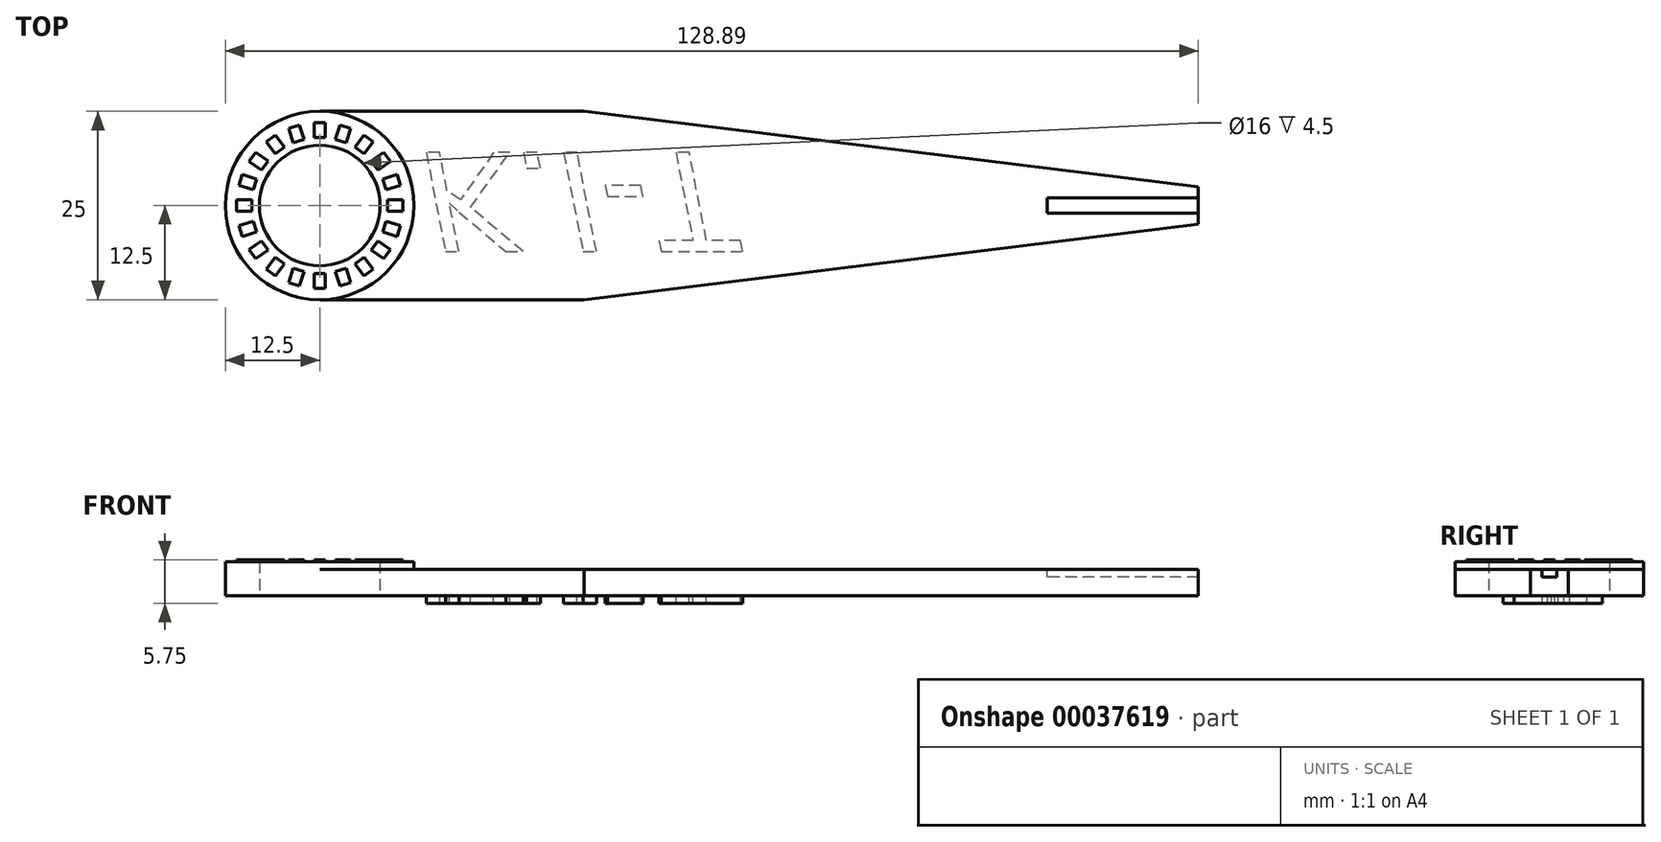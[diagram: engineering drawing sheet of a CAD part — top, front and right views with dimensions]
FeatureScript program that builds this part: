
annotation { "Feature Type Name" : "Feature", "Feature Type Description" : "" }
export const myFeature = defineFeature(function(context is Context, id is Id, definition is map)
    precondition{}
    {
        {
            var Q0;
            Q0=qCreatedBy(makeId("Top.planeOp"),FACE);
            var sketch = newSketch(context, id + "F0", { "sketchPlane" : qUnion([Q0])});
            skCircle(sketch, "E0", {"center": v(0, 0) * mm, "radius": 8 * mm});
            skCircle(sketch, "E1", {"center": v(0, 0) * mm, "radius": 12.5 * mm});
            skPoint(sketch, "E2", {"position": v(0, 12.5) * mm});
            skLineSegment(sketch, "E3", {"start": v(0, 12.5) * mm, "end": v(35, 12.5) * mm});
            skLineSegment(sketch, "E4", {"start": v(0, 0) * mm, "end": v(39.93, 0) * mm, "construction": true});
            skLineSegment(sketch, "E5.MirrorCS", {"start": v(0, -12.5) * mm, "end": v(35, -12.5) * mm});
            skLineSegment(sketch, "E6", {"start": v(35, 12.5) * mm, "end": v(89.7, 12.5) * mm, "construction": true});
            skLineSegment(sketch, "E7", {"start": v(35, 12.5) * mm, "end": v(116.39, 2.5) * mm});
            skLineSegment(sketch, "E8.MirrorCS", {"start": v(35, -12.5) * mm, "end": v(116.39, -2.5) * mm});
            skLineSegment(sketch, "E9", {"start": v(116.39, 2.5) * mm, "end": v(116.39, -2.5) * mm});
            skSolve(sketch);
        }
        {
            var Q0;
            Q0 = qSketchRegion(id + "F0", true);
            extrude(context, id + "F1", {"entities" : qUnion([Q0]), "depth" : 3.5 * mm});
        }
        {
            var Q0;
            Q0=makeQuery(id+"F1.opExtrude","CAP_FACE",FACE,{"disambiguationData":[OSD([sQuery(id+"F0.wireOp",EDGE,"E0"),sQuery(id+"F0.wireOp",EDGE,"E1"),sQuery(id+"F0.wireOp",EDGE,"E3"),sQuery(id+"F0.wireOp",EDGE,"E5.MirrorCS"),sQuery(id+"F0.wireOp",EDGE,"E7"),sQuery(id+"F0.wireOp",EDGE,"E8.MirrorCS"),sQuery(id+"F0.wireOp",EDGE,"E9")])],"isStart":false});
            var sketch = newSketch(context, id + "F2", { "sketchPlane" : qUnion([Q0])});
            skCircle(sketch, "E10", {"center": v(0, 0) * mm, "radius": 12.5 * mm});
            skCircle(sketch, "E11", {"center": v(0, 0) * mm, "radius": 8 * mm});
            skSolve(sketch);
        }
        {
            var Q0;
            Q0 = qSketchRegion(id + "F2", true);
            extrude(context, id + "F3", {"entities" : qUnion([Q0]), "operationType" : NewBodyOperationType.ADD, "depth" : 1 * mm});
        }
        {
            var Q0;
            Q0=makeQuery(id+"F3.opExtrude","CAP_FACE",FACE,{"disambiguationData":[OSD([sQuery(id+"F2.wireOp",EDGE,"E10"),sQuery(id+"F2.wireOp",EDGE,"E11")])],"isStart":false});
            var sketch = newSketch(context, id + "F4", { "sketchPlane" : qUnion([Q0])});
            skLineSegment(sketch, "E12.bottom", {"start": v(-0.75, 11) * mm, "end": v(0.75, 11) * mm});
            skLineSegment(sketch, "E12.top", {"start": v(-0.75, 9) * mm, "end": v(0.75, 9) * mm});
            skLineSegment(sketch, "E12.left", {"start": v(-0.75, 11) * mm, "end": v(-0.75, 9) * mm});
            skLineSegment(sketch, "E12.right", {"start": v(0.75, 11) * mm, "end": v(0.75, 9) * mm});
            skPoint(sketch, "E13", {"position": v(0, 8) * mm});
            skLineSegment(sketch, "E14.1.0", {"start": v(-4.11, 10.23) * mm, "end": v(-2.69, 10.7) * mm});
            skLineSegment(sketch, "E14.1.1", {"start": v(-4.11, 10.23) * mm, "end": v(-3.5, 8.33) * mm});
            skLineSegment(sketch, "E14.1.2", {"start": v(-3.5, 8.33) * mm, "end": v(-2.07, 8.8) * mm});
            skLineSegment(sketch, "E14.1.3", {"start": v(-2.69, 10.7) * mm, "end": v(-2.07, 8.8) * mm});
            skLineSegment(sketch, "E14.2.0", {"start": v(-7.07, 8.46) * mm, "end": v(-5.86, 9.34) * mm});
            skLineSegment(sketch, "E14.2.1", {"start": v(-7.07, 8.46) * mm, "end": v(-5.9, 6.84) * mm});
            skLineSegment(sketch, "E14.2.2", {"start": v(-5.9, 6.84) * mm, "end": v(-4.68, 7.72) * mm});
            skLineSegment(sketch, "E14.2.3", {"start": v(-5.86, 9.34) * mm, "end": v(-4.68, 7.72) * mm});
            skPoint(sketch, "E14.center", {"position": v(0, 0) * mm});
            skLineSegment(sketch, "E15.1.3.0", {"start": v(-9.34, 5.86) * mm, "end": v(-8.46, 7.07) * mm});
            skLineSegment(sketch, "E15.3.3.0", {"start": v(-9.34, 5.86) * mm, "end": v(-7.72, 4.68) * mm});
            skLineSegment(sketch, "E15.6.3.0", {"start": v(-7.72, 4.68) * mm, "end": v(-6.84, 5.9) * mm});
            skLineSegment(sketch, "E15.9.3.0", {"start": v(-8.46, 7.07) * mm, "end": v(-6.84, 5.9) * mm});
            skLineSegment(sketch, "E15.1.4.0", {"start": v(-10.7, 2.69) * mm, "end": v(-10.23, 4.11) * mm});
            skLineSegment(sketch, "E15.3.4.0", {"start": v(-10.7, 2.69) * mm, "end": v(-8.8, 2.07) * mm});
            skLineSegment(sketch, "E15.6.4.0", {"start": v(-8.8, 2.07) * mm, "end": v(-8.33, 3.5) * mm});
            skLineSegment(sketch, "E15.9.4.0", {"start": v(-10.23, 4.11) * mm, "end": v(-8.33, 3.5) * mm});
            skLineSegment(sketch, "E15.1.5.0", {"start": v(-11, -0.75) * mm, "end": v(-11, 0.75) * mm});
            skLineSegment(sketch, "E15.3.5.0", {"start": v(-11, -0.75) * mm, "end": v(-9, -0.75) * mm});
            skLineSegment(sketch, "E15.6.5.0", {"start": v(-9, -0.75) * mm, "end": v(-9, 0.75) * mm});
            skLineSegment(sketch, "E15.9.5.0", {"start": v(-11, 0.75) * mm, "end": v(-9, 0.75) * mm});
            skLineSegment(sketch, "E15.1.6.0", {"start": v(-10.23, -4.11) * mm, "end": v(-10.7, -2.69) * mm});
            skLineSegment(sketch, "E15.3.6.0", {"start": v(-10.23, -4.11) * mm, "end": v(-8.33, -3.5) * mm});
            skLineSegment(sketch, "E15.6.6.0", {"start": v(-8.33, -3.5) * mm, "end": v(-8.8, -2.07) * mm});
            skLineSegment(sketch, "E15.9.6.0", {"start": v(-10.7, -2.69) * mm, "end": v(-8.8, -2.07) * mm});
            skLineSegment(sketch, "E15.1.7.0", {"start": v(-8.46, -7.07) * mm, "end": v(-9.34, -5.86) * mm});
            skLineSegment(sketch, "E15.3.7.0", {"start": v(-8.46, -7.07) * mm, "end": v(-6.84, -5.9) * mm});
            skLineSegment(sketch, "E15.6.7.0", {"start": v(-6.84, -5.9) * mm, "end": v(-7.72, -4.68) * mm});
            skLineSegment(sketch, "E15.9.7.0", {"start": v(-9.34, -5.86) * mm, "end": v(-7.72, -4.68) * mm});
            skLineSegment(sketch, "E15.1.8.0", {"start": v(-5.86, -9.34) * mm, "end": v(-7.07, -8.46) * mm});
            skLineSegment(sketch, "E15.3.8.0", {"start": v(-5.86, -9.34) * mm, "end": v(-4.68, -7.72) * mm});
            skLineSegment(sketch, "E15.6.8.0", {"start": v(-4.68, -7.72) * mm, "end": v(-5.9, -6.84) * mm});
            skLineSegment(sketch, "E15.9.8.0", {"start": v(-7.07, -8.46) * mm, "end": v(-5.9, -6.84) * mm});
            skLineSegment(sketch, "E15.1.9.0", {"start": v(-2.69, -10.7) * mm, "end": v(-4.11, -10.23) * mm});
            skLineSegment(sketch, "E15.3.9.0", {"start": v(-2.69, -10.7) * mm, "end": v(-2.07, -8.8) * mm});
            skLineSegment(sketch, "E15.6.9.0", {"start": v(-2.07, -8.8) * mm, "end": v(-3.5, -8.33) * mm});
            skLineSegment(sketch, "E15.9.9.0", {"start": v(-4.11, -10.23) * mm, "end": v(-3.5, -8.33) * mm});
            skLineSegment(sketch, "E15.1.10.0", {"start": v(0.75, -11) * mm, "end": v(-0.75, -11) * mm});
            skLineSegment(sketch, "E15.3.10.0", {"start": v(0.75, -11) * mm, "end": v(0.75, -9) * mm});
            skLineSegment(sketch, "E15.6.10.0", {"start": v(0.75, -9) * mm, "end": v(-0.75, -9) * mm});
            skLineSegment(sketch, "E15.9.10.0", {"start": v(-0.75, -11) * mm, "end": v(-0.75, -9) * mm});
            skLineSegment(sketch, "E15.1.11.0", {"start": v(4.11, -10.23) * mm, "end": v(2.69, -10.7) * mm});
            skLineSegment(sketch, "E15.3.11.0", {"start": v(4.11, -10.23) * mm, "end": v(3.5, -8.33) * mm});
            skLineSegment(sketch, "E15.6.11.0", {"start": v(3.5, -8.33) * mm, "end": v(2.07, -8.8) * mm});
            skLineSegment(sketch, "E15.9.11.0", {"start": v(2.69, -10.7) * mm, "end": v(2.07, -8.8) * mm});
            skLineSegment(sketch, "E15.1.12.0", {"start": v(7.07, -8.46) * mm, "end": v(5.86, -9.34) * mm});
            skLineSegment(sketch, "E15.3.12.0", {"start": v(7.07, -8.46) * mm, "end": v(5.9, -6.84) * mm});
            skLineSegment(sketch, "E15.6.12.0", {"start": v(5.9, -6.84) * mm, "end": v(4.68, -7.72) * mm});
            skLineSegment(sketch, "E15.9.12.0", {"start": v(5.86, -9.34) * mm, "end": v(4.68, -7.72) * mm});
            skLineSegment(sketch, "E15.1.13.0", {"start": v(9.34, -5.86) * mm, "end": v(8.46, -7.07) * mm});
            skLineSegment(sketch, "E15.3.13.0", {"start": v(9.34, -5.86) * mm, "end": v(7.72, -4.68) * mm});
            skLineSegment(sketch, "E15.6.13.0", {"start": v(7.72, -4.68) * mm, "end": v(6.84, -5.9) * mm});
            skLineSegment(sketch, "E15.9.13.0", {"start": v(8.46, -7.07) * mm, "end": v(6.84, -5.9) * mm});
            skLineSegment(sketch, "E15.1.14.0", {"start": v(10.7, -2.69) * mm, "end": v(10.23, -4.11) * mm});
            skLineSegment(sketch, "E15.3.14.0", {"start": v(10.7, -2.69) * mm, "end": v(8.8, -2.07) * mm});
            skLineSegment(sketch, "E15.6.14.0", {"start": v(8.8, -2.07) * mm, "end": v(8.33, -3.5) * mm});
            skLineSegment(sketch, "E15.9.14.0", {"start": v(10.23, -4.11) * mm, "end": v(8.33, -3.5) * mm});
            skLineSegment(sketch, "E15.1.15.0", {"start": v(11, 0.75) * mm, "end": v(11, -0.75) * mm});
            skLineSegment(sketch, "E15.3.15.0", {"start": v(11, 0.75) * mm, "end": v(9, 0.75) * mm});
            skLineSegment(sketch, "E15.6.15.0", {"start": v(9, 0.75) * mm, "end": v(9, -0.75) * mm});
            skLineSegment(sketch, "E15.9.15.0", {"start": v(11, -0.75) * mm, "end": v(9, -0.75) * mm});
            skLineSegment(sketch, "E15.1.16.0", {"start": v(10.23, 4.11) * mm, "end": v(10.7, 2.69) * mm});
            skLineSegment(sketch, "E15.3.16.0", {"start": v(10.23, 4.11) * mm, "end": v(8.33, 3.5) * mm});
            skLineSegment(sketch, "E15.6.16.0", {"start": v(8.33, 3.5) * mm, "end": v(8.8, 2.07) * mm});
            skLineSegment(sketch, "E15.9.16.0", {"start": v(10.7, 2.69) * mm, "end": v(8.8, 2.07) * mm});
            skLineSegment(sketch, "E15.1.17.0", {"start": v(8.46, 7.07) * mm, "end": v(9.34, 5.86) * mm});
            skLineSegment(sketch, "E15.3.17.0", {"start": v(8.46, 7.07) * mm, "end": v(6.84, 5.9) * mm});
            skLineSegment(sketch, "E15.6.17.0", {"start": v(6.84, 5.9) * mm, "end": v(7.72, 4.68) * mm});
            skLineSegment(sketch, "E15.9.17.0", {"start": v(9.34, 5.86) * mm, "end": v(7.72, 4.68) * mm});
            skLineSegment(sketch, "E15.1.18.0", {"start": v(5.86, 9.34) * mm, "end": v(7.07, 8.46) * mm});
            skLineSegment(sketch, "E15.3.18.0", {"start": v(5.86, 9.34) * mm, "end": v(4.68, 7.72) * mm});
            skLineSegment(sketch, "E15.6.18.0", {"start": v(4.68, 7.72) * mm, "end": v(5.9, 6.84) * mm});
            skLineSegment(sketch, "E15.9.18.0", {"start": v(7.07, 8.46) * mm, "end": v(5.9, 6.84) * mm});
            skLineSegment(sketch, "E15.1.19.0", {"start": v(2.69, 10.7) * mm, "end": v(4.11, 10.23) * mm});
            skLineSegment(sketch, "E15.3.19.0", {"start": v(2.69, 10.7) * mm, "end": v(2.07, 8.8) * mm});
            skLineSegment(sketch, "E15.6.19.0", {"start": v(2.07, 8.8) * mm, "end": v(3.5, 8.33) * mm});
            skLineSegment(sketch, "E15.9.19.0", {"start": v(4.11, 10.23) * mm, "end": v(3.5, 8.33) * mm});
            skSolve(sketch);
        }
        {
            var Q0;
            Q0 = qSketchRegion(id + "F4", true);
            extrude(context, id + "F5", {"entities" : qUnion([Q0]), "operationType" : NewBodyOperationType.ADD, "depth" : .25 * mm});
        }
        {
            var Q0;
            Q0=makeQuery(id+"F1.opExtrude","CAP_FACE",FACE,{"disambiguationData":[OSD([sQuery(id+"F0.wireOp",EDGE,"E0"),sQuery(id+"F0.wireOp",EDGE,"E1"),sQuery(id+"F0.wireOp",EDGE,"E3"),sQuery(id+"F0.wireOp",EDGE,"E5.MirrorCS"),sQuery(id+"F0.wireOp",EDGE,"E7"),sQuery(id+"F0.wireOp",EDGE,"E8.MirrorCS"),sQuery(id+"F0.wireOp",EDGE,"E9")])],"isStart":false});
            var sketch = newSketch(context, id + "F6", { "sketchPlane" : qUnion([Q0])});
            skLineSegment(sketch, "E16.bottom", {"start": v(116.39, 1) * mm, "end": v(96.39, 1) * mm});
            skLineSegment(sketch, "E16.top", {"start": v(116.39, -1) * mm, "end": v(96.39, -1) * mm});
            skLineSegment(sketch, "E16.left", {"start": v(116.39, 1) * mm, "end": v(116.39, -1) * mm});
            skLineSegment(sketch, "E16.right", {"start": v(96.39, 1) * mm, "end": v(96.39, -1) * mm});
            skSolve(sketch);
        }
        {
            var Q0;
            Q0 = qSketchRegion(id + "F6", true);
            extrude(context, id + "F7", {"entities" : qUnion([Q0]), "operationType" : NewBodyOperationType.REMOVE, "oppositeDirection" : true, "depth" : 1 * mm});
        }
        {
            var Q0;
            Q0=makeQuery(id+"F1.opExtrude","CAP_FACE",FACE,{"disambiguationData":[OSD([sQuery(id+"F0.wireOp",EDGE,"E0"),sQuery(id+"F0.wireOp",EDGE,"E1"),sQuery(id+"F0.wireOp",EDGE,"E3"),sQuery(id+"F0.wireOp",EDGE,"E5.MirrorCS"),sQuery(id+"F0.wireOp",EDGE,"E7"),sQuery(id+"F0.wireOp",EDGE,"E8.MirrorCS"),sQuery(id+"F0.wireOp",EDGE,"E9")])],"isStart":true});
            var sketch = newSketch(context, id + "F8", { "sketchPlane" : qUnion([Q0])});
            skText(sketch, "E17", { "text": "K.I-T", "fontName": "Arimo-Italic.ttf"});
            const initialGuessF8  = {"E17": [0.01352, -0.00702, 1, 0, 0.01375]};
            skSetInitialGuess(sketch, initialGuessF8);
            skSolve(sketch);
        }
        {
            var Q0;
            Q0 = qSketchRegion(id + "F8", true);
            extrude(context, id + "F9", {"entities" : qUnion([Q0]), "operationType" : NewBodyOperationType.ADD, "depth" : 1 * mm});
        }
    });
